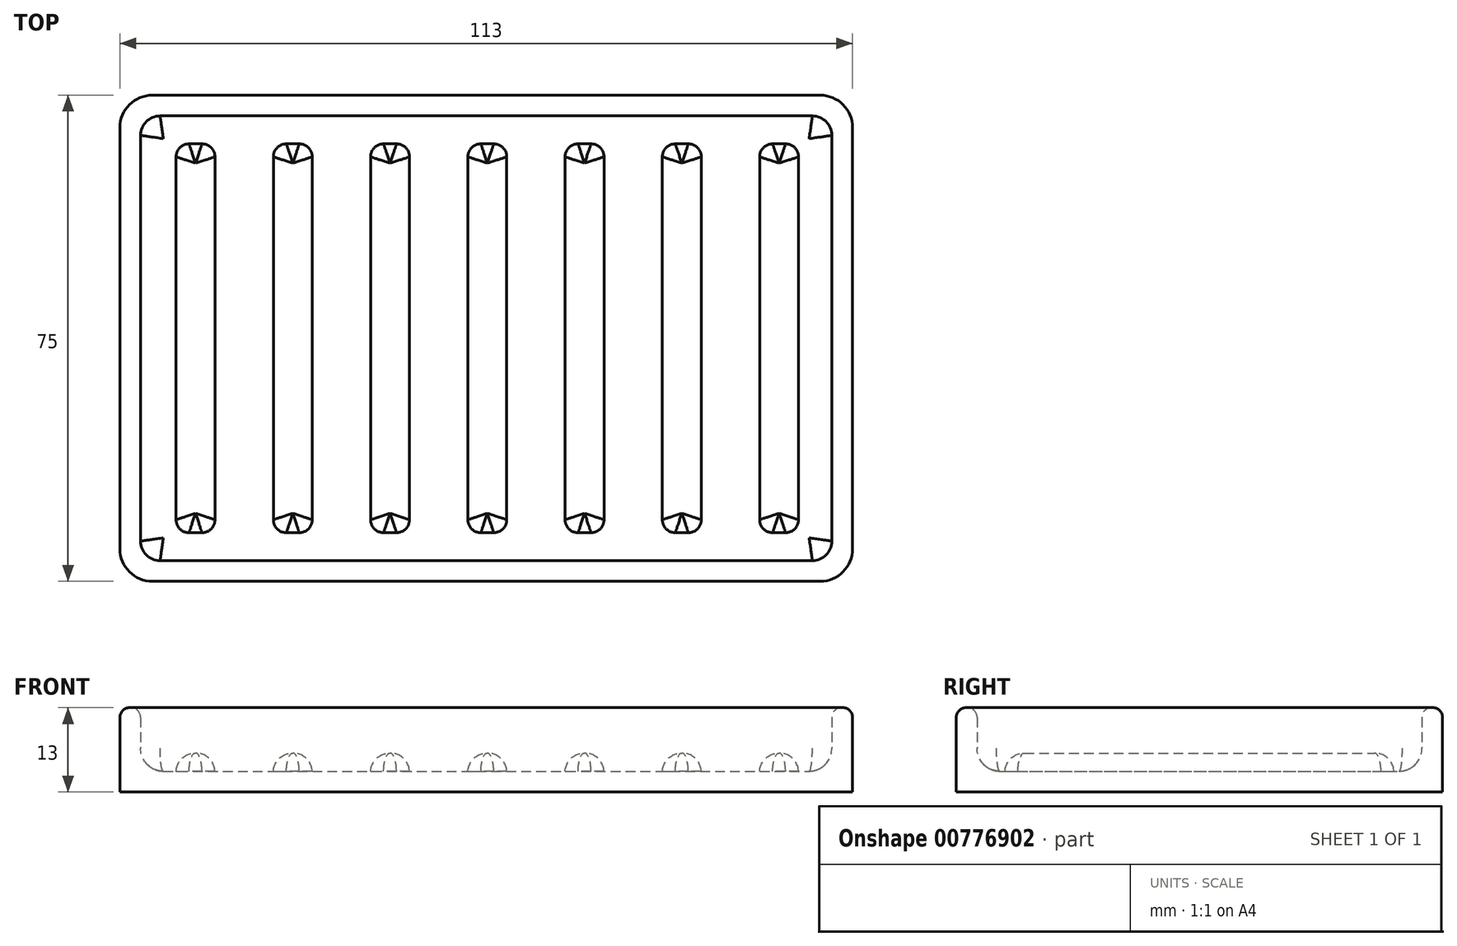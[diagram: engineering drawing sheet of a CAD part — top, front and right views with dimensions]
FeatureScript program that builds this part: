
annotation { "Feature Type Name" : "Feature", "Feature Type Description" : "" }
export const myFeature = defineFeature(function(context is Context, id is Id, definition is map)
    precondition{}
    {
        {
            var Q0;
            Q0=qCreatedBy(makeId("Top.planeOp"),FACE);
            var sketch = newSketch(context, id + "F0", { "sketchPlane" : qUnion([Q0])});
            skLineSegment(sketch, "E0.bottom", {"start": v(51.5, 37.5) * mm, "end": v(-51.5, 37.5) * mm});
            skLineSegment(sketch, "E0.top", {"start": v(51.5, -37.5) * mm, "end": v(-51.5, -37.5) * mm});
            skLineSegment(sketch, "E0.left", {"start": v(56.5, 32.5) * mm, "end": v(56.5, -32.5) * mm});
            skLineSegment(sketch, "E0.right", {"start": v(-56.5, 32.5) * mm, "end": v(-56.5, -32.5) * mm});
            skLineSegment(sketch, "E1.0", {"start": v(-53.3, 31.3) * mm, "end": v(-53.3, -31.3) * mm});
            skLineSegment(sketch, "E1.1", {"start": v(50.3, 34.3) * mm, "end": v(-50.3, 34.3) * mm});
            skLineSegment(sketch, "E1.2", {"start": v(53.3, 31.3) * mm, "end": v(53.3, -31.3) * mm});
            skLineSegment(sketch, "E1.3", {"start": v(50.3, -34.3) * mm, "end": v(-50.3, -34.3) * mm});
            skLineSegment(sketch, "E2.bottom", {"start": v(-45.84, 30) * mm, "end": v(-43.84, 30) * mm});
            skLineSegment(sketch, "E2.top", {"start": v(-45.84, -30) * mm, "end": v(-43.84, -30) * mm});
            skLineSegment(sketch, "E2.left", {"start": v(-47.84, 28) * mm, "end": v(-47.84, -28) * mm});
            skLineSegment(sketch, "E2.right", {"start": v(-41.84, 28) * mm, "end": v(-41.84, -28) * mm});
            skPoint(sketch, "E3.visualSharp", {"position": v(-56.5, 37.5) * mm});
            skArc(sketch, "E3.filletArc", {"start": v(-51.5, 37.5) * mm, "mid": v(-55.04, 36.04) * mm, "end": v(-56.5, 32.5) * mm});
            skPoint(sketch, "E4.visualSharp", {"position": v(-47.84, 30) * mm});
            skArc(sketch, "E4.filletArc", {"start": v(-45.84, 30) * mm, "mid": v(-47.25, 29.4) * mm, "end": v(-47.84, 28) * mm});
            skPoint(sketch, "E5.visualSharp", {"position": v(-47.84, -30) * mm});
            skArc(sketch, "E5.filletArc", {"start": v(-47.84, -28) * mm, "mid": v(-47.25, -29.42) * mm, "end": v(-45.84, -30) * mm});
            skPoint(sketch, "E6.visualSharp", {"position": v(-41.84, 30) * mm});
            skArc(sketch, "E6.filletArc", {"start": v(-41.84, 28) * mm, "mid": v(-42.42, 29.4) * mm, "end": v(-43.84, 30) * mm});
            skPoint(sketch, "E7.visualSharp", {"position": v(-41.84, -30) * mm});
            skArc(sketch, "E7.filletArc", {"start": v(-43.84, -30) * mm, "mid": v(-42.42, -29.42) * mm, "end": v(-41.84, -28) * mm});
            skPoint(sketch, "E8.1.0.0", {"position": v(-32.84, 30) * mm});
            skPoint(sketch, "E8.1.0.1", {"position": v(-32.84, -30) * mm});
            skPoint(sketch, "E8.1.0.2", {"position": v(-26.84, 30) * mm});
            skPoint(sketch, "E8.1.0.3", {"position": v(-26.84, -30) * mm});
            skLineSegment(sketch, "E8.1.0.4", {"start": v(-30.84, 30) * mm, "end": v(-28.84, 30) * mm});
            skLineSegment(sketch, "E8.1.0.5", {"start": v(-30.84, -30) * mm, "end": v(-28.84, -30) * mm});
            skLineSegment(sketch, "E8.1.0.6", {"start": v(-32.84, 28) * mm, "end": v(-32.84, -28) * mm});
            skLineSegment(sketch, "E8.1.0.7", {"start": v(-26.84, 28) * mm, "end": v(-26.84, -28) * mm});
            skArc(sketch, "E8.1.0.8", {"start": v(-30.84, 30) * mm, "mid": v(-32.25, 29.4) * mm, "end": v(-32.84, 28) * mm});
            skArc(sketch, "E8.1.0.9", {"start": v(-32.84, -28) * mm, "mid": v(-32.25, -29.42) * mm, "end": v(-30.84, -30) * mm});
            skArc(sketch, "E8.1.0.10", {"start": v(-26.84, 28) * mm, "mid": v(-27.42, 29.4) * mm, "end": v(-28.84, 30) * mm});
            skArc(sketch, "E8.1.0.11", {"start": v(-28.84, -30) * mm, "mid": v(-27.42, -29.42) * mm, "end": v(-26.84, -28) * mm});
            skPoint(sketch, "E8.2.0.0", {"position": v(-17.84, 30) * mm});
            skPoint(sketch, "E8.2.0.1", {"position": v(-17.84, -30) * mm});
            skPoint(sketch, "E8.2.0.2", {"position": v(-11.84, 30) * mm});
            skPoint(sketch, "E8.2.0.3", {"position": v(-11.84, -30) * mm});
            skLineSegment(sketch, "E8.2.0.4", {"start": v(-15.84, 30) * mm, "end": v(-13.84, 30) * mm});
            skLineSegment(sketch, "E8.2.0.5", {"start": v(-15.84, -30) * mm, "end": v(-13.84, -30) * mm});
            skLineSegment(sketch, "E8.2.0.6", {"start": v(-17.84, 28) * mm, "end": v(-17.84, -28) * mm});
            skLineSegment(sketch, "E8.2.0.7", {"start": v(-11.84, 28) * mm, "end": v(-11.84, -28) * mm});
            skArc(sketch, "E8.2.0.8", {"start": v(-15.84, 30) * mm, "mid": v(-17.25, 29.4) * mm, "end": v(-17.84, 28) * mm});
            skArc(sketch, "E8.2.0.9", {"start": v(-17.84, -28) * mm, "mid": v(-17.25, -29.42) * mm, "end": v(-15.84, -30) * mm});
            skArc(sketch, "E8.2.0.10", {"start": v(-11.84, 28) * mm, "mid": v(-12.42, 29.4) * mm, "end": v(-13.84, 30) * mm});
            skArc(sketch, "E8.2.0.11", {"start": v(-13.84, -30) * mm, "mid": v(-12.42, -29.42) * mm, "end": v(-11.84, -28) * mm});
            skPoint(sketch, "E8.3.0.0", {"position": v(-2.84, 30) * mm});
            skPoint(sketch, "E8.3.0.1", {"position": v(-2.84, -30) * mm});
            skPoint(sketch, "E8.3.0.2", {"position": v(3.16, 30) * mm});
            skPoint(sketch, "E8.3.0.3", {"position": v(3.16, -30) * mm});
            skLineSegment(sketch, "E8.3.0.4", {"start": v(-0.84, 30) * mm, "end": v(1.16, 30) * mm});
            skLineSegment(sketch, "E8.3.0.5", {"start": v(-0.84, -30) * mm, "end": v(1.16, -30) * mm});
            skLineSegment(sketch, "E8.3.0.6", {"start": v(-2.84, 28) * mm, "end": v(-2.84, -28) * mm});
            skLineSegment(sketch, "E8.3.0.7", {"start": v(3.16, 28) * mm, "end": v(3.16, -28) * mm});
            skArc(sketch, "E8.3.0.8", {"start": v(-0.84, 30) * mm, "mid": v(-2.25, 29.4) * mm, "end": v(-2.84, 28) * mm});
            skArc(sketch, "E8.3.0.9", {"start": v(-2.84, -28) * mm, "mid": v(-2.25, -29.42) * mm, "end": v(-0.84, -30) * mm});
            skArc(sketch, "E8.3.0.10", {"start": v(3.16, 28) * mm, "mid": v(2.58, 29.4) * mm, "end": v(1.16, 30) * mm});
            skArc(sketch, "E8.3.0.11", {"start": v(1.16, -30) * mm, "mid": v(2.58, -29.42) * mm, "end": v(3.16, -28) * mm});
            skPoint(sketch, "E8.4.0.0", {"position": v(12.16, 30) * mm});
            skPoint(sketch, "E8.4.0.1", {"position": v(12.16, -30) * mm});
            skPoint(sketch, "E8.4.0.2", {"position": v(18.16, 30) * mm});
            skPoint(sketch, "E8.4.0.3", {"position": v(18.16, -30) * mm});
            skLineSegment(sketch, "E8.4.0.4", {"start": v(14.16, 30) * mm, "end": v(16.16, 30) * mm});
            skLineSegment(sketch, "E8.4.0.5", {"start": v(14.16, -30) * mm, "end": v(16.16, -30) * mm});
            skLineSegment(sketch, "E8.4.0.6", {"start": v(12.16, 28) * mm, "end": v(12.16, -28) * mm});
            skLineSegment(sketch, "E8.4.0.7", {"start": v(18.16, 28) * mm, "end": v(18.16, -28) * mm});
            skArc(sketch, "E8.4.0.8", {"start": v(14.16, 30) * mm, "mid": v(12.75, 29.4) * mm, "end": v(12.16, 28) * mm});
            skArc(sketch, "E8.4.0.9", {"start": v(12.16, -28) * mm, "mid": v(12.75, -29.42) * mm, "end": v(14.16, -30) * mm});
            skArc(sketch, "E8.4.0.10", {"start": v(18.16, 28) * mm, "mid": v(17.58, 29.4) * mm, "end": v(16.16, 30) * mm});
            skArc(sketch, "E8.4.0.11", {"start": v(16.16, -30) * mm, "mid": v(17.58, -29.42) * mm, "end": v(18.16, -28) * mm});
            skPoint(sketch, "E8.5.0.0", {"position": v(27.16, 30) * mm});
            skPoint(sketch, "E8.5.0.1", {"position": v(27.16, -30) * mm});
            skPoint(sketch, "E8.5.0.2", {"position": v(33.16, 30) * mm});
            skPoint(sketch, "E8.5.0.3", {"position": v(33.16, -30) * mm});
            skLineSegment(sketch, "E8.5.0.4", {"start": v(29.16, 30) * mm, "end": v(31.16, 30) * mm});
            skLineSegment(sketch, "E8.5.0.5", {"start": v(29.16, -30) * mm, "end": v(31.16, -30) * mm});
            skLineSegment(sketch, "E8.5.0.6", {"start": v(27.16, 28) * mm, "end": v(27.16, -28) * mm});
            skLineSegment(sketch, "E8.5.0.7", {"start": v(33.16, 28) * mm, "end": v(33.16, -28) * mm});
            skArc(sketch, "E8.5.0.8", {"start": v(29.16, 30) * mm, "mid": v(27.75, 29.4) * mm, "end": v(27.16, 28) * mm});
            skArc(sketch, "E8.5.0.9", {"start": v(27.16, -28) * mm, "mid": v(27.75, -29.42) * mm, "end": v(29.16, -30) * mm});
            skArc(sketch, "E8.5.0.10", {"start": v(33.16, 28) * mm, "mid": v(32.58, 29.4) * mm, "end": v(31.16, 30) * mm});
            skArc(sketch, "E8.5.0.11", {"start": v(31.16, -30) * mm, "mid": v(32.58, -29.42) * mm, "end": v(33.16, -28) * mm});
            skPoint(sketch, "E8.6.0.0", {"position": v(42.16, 30) * mm});
            skPoint(sketch, "E8.6.0.1", {"position": v(42.16, -30) * mm});
            skPoint(sketch, "E8.6.0.2", {"position": v(48.16, 30) * mm});
            skPoint(sketch, "E8.6.0.3", {"position": v(48.16, -30) * mm});
            skLineSegment(sketch, "E8.6.0.4", {"start": v(44.16, 30) * mm, "end": v(46.16, 30) * mm});
            skLineSegment(sketch, "E8.6.0.5", {"start": v(44.16, -30) * mm, "end": v(46.16, -30) * mm});
            skLineSegment(sketch, "E8.6.0.6", {"start": v(42.16, 28) * mm, "end": v(42.16, -28) * mm});
            skLineSegment(sketch, "E8.6.0.7", {"start": v(48.16, 28) * mm, "end": v(48.16, -28) * mm});
            skArc(sketch, "E8.6.0.8", {"start": v(44.16, 30) * mm, "mid": v(42.75, 29.4) * mm, "end": v(42.16, 28) * mm});
            skArc(sketch, "E8.6.0.9", {"start": v(42.16, -28) * mm, "mid": v(42.75, -29.42) * mm, "end": v(44.16, -30) * mm});
            skArc(sketch, "E8.6.0.10", {"start": v(48.16, 28) * mm, "mid": v(47.58, 29.4) * mm, "end": v(46.16, 30) * mm});
            skArc(sketch, "E8.6.0.11", {"start": v(46.16, -30) * mm, "mid": v(47.58, -29.42) * mm, "end": v(48.16, -28) * mm});
            skLineSegment(sketch, "E8.direction1", {"start": v(-47.84, -30) * mm, "end": v(-32.84, -30) * mm, "construction": true});
            skPoint(sketch, "E9.visualSharp", {"position": v(-56.5, -37.5) * mm});
            skArc(sketch, "E9.filletArc", {"start": v(-56.5, -32.5) * mm, "mid": v(-55.04, -36.04) * mm, "end": v(-51.5, -37.5) * mm});
            skPoint(sketch, "E10.visualSharp", {"position": v(56.5, -37.5) * mm});
            skArc(sketch, "E10.filletArc", {"start": v(51.5, -37.5) * mm, "mid": v(55.04, -36.04) * mm, "end": v(56.5, -32.5) * mm});
            skPoint(sketch, "E11.visualSharp", {"position": v(56.5, 37.5) * mm});
            skArc(sketch, "E11.filletArc", {"start": v(56.5, 32.5) * mm, "mid": v(55.04, 36.04) * mm, "end": v(51.5, 37.5) * mm});
            skPoint(sketch, "E12.visualSharp", {"position": v(-53.3, -34.3) * mm});
            skArc(sketch, "E12.filletArc", {"start": v(-53.3, -31.3) * mm, "mid": v(-52.42, -33.42) * mm, "end": v(-50.3, -34.3) * mm});
            skPoint(sketch, "E13.visualSharp", {"position": v(-53.3, 34.3) * mm});
            skArc(sketch, "E13.filletArc", {"start": v(-50.3, 34.3) * mm, "mid": v(-52.42, 33.42) * mm, "end": v(-53.3, 31.3) * mm});
            skPoint(sketch, "E14.visualSharp", {"position": v(53.3, 34.3) * mm});
            skArc(sketch, "E14.filletArc", {"start": v(53.3, 31.3) * mm, "mid": v(52.42, 33.42) * mm, "end": v(50.3, 34.3) * mm});
            skPoint(sketch, "E15.visualSharp", {"position": v(53.3, -34.3) * mm});
            skArc(sketch, "E15.filletArc", {"start": v(50.3, -34.3) * mm, "mid": v(52.42, -33.42) * mm, "end": v(53.3, -31.3) * mm});
            skSolve(sketch);
        }
        {
            var Q0;
            Q0=makeQuery(id+"F0.imprint","IMPRINT",FACE,{"disambiguationData":[TD([[makeQuery(id+"F0.imprint","IMPRINT",EDGE,{"derivedFrom":sQuery(id+"F0.wireOp",EDGE,"E1.0")}),1.0]])]});
            var Q1;
            Q1=makeQuery(id+"F0.imprint","IMPRINT",FACE,{"disambiguationData":[TD([[makeQuery(id+"F0.imprint","IMPRINT",EDGE,{"derivedFrom":sQuery(id+"F0.wireOp",EDGE,"E8.6.0.4")}),-1.0]])]});
            var Q2;
            Q2=makeQuery(id+"F0.imprint","IMPRINT",FACE,{"disambiguationData":[TD([[makeQuery(id+"F0.imprint","IMPRINT",EDGE,{"derivedFrom":sQuery(id+"F0.wireOp",EDGE,"E8.5.0.4")}),-1.0]])]});
            var Q3;
            Q3=makeQuery(id+"F0.imprint","IMPRINT",FACE,{"disambiguationData":[TD([[makeQuery(id+"F0.imprint","IMPRINT",EDGE,{"derivedFrom":sQuery(id+"F0.wireOp",EDGE,"E8.4.0.4")}),-1.0]])]});
            var Q4;
            Q4=makeQuery(id+"F0.imprint","IMPRINT",FACE,{"disambiguationData":[TD([[makeQuery(id+"F0.imprint","IMPRINT",EDGE,{"derivedFrom":sQuery(id+"F0.wireOp",EDGE,"E8.3.0.4")}),-1.0]])]});
            var Q5;
            Q5=makeQuery(id+"F0.imprint","IMPRINT",FACE,{"disambiguationData":[TD([[makeQuery(id+"F0.imprint","IMPRINT",EDGE,{"derivedFrom":sQuery(id+"F0.wireOp",EDGE,"E8.2.0.4")}),-1.0]])]});
            var Q6;
            Q6=makeQuery(id+"F0.imprint","IMPRINT",FACE,{"disambiguationData":[TD([[makeQuery(id+"F0.imprint","IMPRINT",EDGE,{"derivedFrom":sQuery(id+"F0.wireOp",EDGE,"E8.1.0.4")}),-1.0]])]});
            var Q7;
            Q7=makeQuery(id+"F0.imprint","IMPRINT",FACE,{"disambiguationData":[TD([[makeQuery(id+"F0.imprint","IMPRINT",EDGE,{"derivedFrom":sQuery(id+"F0.wireOp",EDGE,"E2.bottom")}),-1.0]])]});
            var Q8;
            Q8=makeQuery(id+"F0.imprint","IMPRINT",FACE,{"disambiguationData":[TD([[makeQuery(id+"F0.imprint","IMPRINT",EDGE,{"derivedFrom":sQuery(id+"F0.wireOp",EDGE,"E0.bottom")}),1.0]])]});
            extrude(context, id + "F1", {"entities" : qUnion([Q0, Q1, Q2, Q3, Q4, Q5, Q6, Q7, Q8]), "depth" : 3.2 * mm, "offsetDistance" : 25 * mm});
        }
        {
            var Q0;
            Q0=makeQuery(id+"F0.imprint","IMPRINT",FACE,{"disambiguationData":[TD([[makeQuery(id+"F0.imprint","IMPRINT",EDGE,{"derivedFrom":sQuery(id+"F0.wireOp",EDGE,"E2.bottom")}),-1.0]])]});
            extrude(context, id + "F2", {"entities" : qUnion([Q0]), "operationType" : NewBodyOperationType.ADD, "depth" : 6 * mm, "offsetDistance" : 25 * mm});
        }
        {
            var Q0;
            Q0=makeQuery(id+"F0.imprint","IMPRINT",FACE,{"disambiguationData":[TD([[makeQuery(id+"F0.imprint","IMPRINT",EDGE,{"derivedFrom":sQuery(id+"F0.wireOp",EDGE,"E8.1.0.4")}),-1.0]])]});
            var Q1;
            Q1=makeQuery(id+"F0.imprint","IMPRINT",FACE,{"disambiguationData":[TD([[makeQuery(id+"F0.imprint","IMPRINT",EDGE,{"derivedFrom":sQuery(id+"F0.wireOp",EDGE,"E8.2.0.4")}),-1.0]])]});
            var Q2;
            Q2=makeQuery(id+"F0.imprint","IMPRINT",FACE,{"disambiguationData":[TD([[makeQuery(id+"F0.imprint","IMPRINT",EDGE,{"derivedFrom":sQuery(id+"F0.wireOp",EDGE,"E8.3.0.4")}),-1.0]])]});
            var Q3;
            Q3=makeQuery(id+"F0.imprint","IMPRINT",FACE,{"disambiguationData":[TD([[makeQuery(id+"F0.imprint","IMPRINT",EDGE,{"derivedFrom":sQuery(id+"F0.wireOp",EDGE,"E8.4.0.4")}),-1.0]])]});
            var Q4;
            Q4=makeQuery(id+"F0.imprint","IMPRINT",FACE,{"disambiguationData":[TD([[makeQuery(id+"F0.imprint","IMPRINT",EDGE,{"derivedFrom":sQuery(id+"F0.wireOp",EDGE,"E8.5.0.4")}),-1.0]])]});
            var Q5;
            Q5=makeQuery(id+"F0.imprint","IMPRINT",FACE,{"disambiguationData":[TD([[makeQuery(id+"F0.imprint","IMPRINT",EDGE,{"derivedFrom":sQuery(id+"F0.wireOp",EDGE,"E8.6.0.4")}),-1.0]])]});
            extrude(context, id + "F3", {"entities" : qUnion([Q0, Q1, Q2, Q3, Q4, Q5]), "operationType" : NewBodyOperationType.ADD, "depth" : 6 * mm, "offsetDistance" : 25 * mm});
        }
        {
            var Q0;
            Q0=makeQuery(id+"F2.opExtrude","CAP_EDGE",EDGE,{"disambiguationData":[OSD([sQuery(id+"F0.wireOp",EDGE,"E2.left")])],"isStart":false});
            var Q1;
            Q1=makeQuery(id+"F3.opExtrude","CAP_EDGE",EDGE,{"disambiguationData":[OSD([sQuery(id+"F0.wireOp",EDGE,"E8.1.0.6")])],"isStart":false});
            var Q2;
            Q2=makeQuery(id+"F3.opExtrude","CAP_EDGE",EDGE,{"disambiguationData":[OSD([sQuery(id+"F0.wireOp",EDGE,"E8.2.0.6")])],"isStart":false});
            var Q3;
            Q3=makeQuery(id+"F3.opExtrude","CAP_EDGE",EDGE,{"disambiguationData":[OSD([sQuery(id+"F0.wireOp",EDGE,"E8.3.0.6")])],"isStart":false});
            var Q4;
            Q4=makeQuery(id+"F3.opExtrude","CAP_EDGE",EDGE,{"disambiguationData":[OSD([sQuery(id+"F0.wireOp",EDGE,"E8.4.0.6")])],"isStart":false});
            var Q5;
            Q5=makeQuery(id+"F3.opExtrude","CAP_EDGE",EDGE,{"disambiguationData":[OSD([sQuery(id+"F0.wireOp",EDGE,"E8.5.0.6")])],"isStart":false});
            var Q6;
            Q6=makeQuery(id+"F3.opExtrude","CAP_EDGE",EDGE,{"disambiguationData":[OSD([sQuery(id+"F0.wireOp",EDGE,"E8.6.0.6")])],"isStart":false});
            fillet(context, id + "F4", {"entities" : qUnion([Q0, Q1, Q2, Q3, Q4, Q5, Q6]), "radius" : 3 * mm, "tangentPropagation" : true, "allowEdgeOverflow" : false});
        }
        {
            var Q0;
            Q0=makeQuery(id+"F0.imprint","IMPRINT",FACE,{"disambiguationData":[TD([[makeQuery(id+"F0.imprint","IMPRINT",EDGE,{"derivedFrom":sQuery(id+"F0.wireOp",EDGE,"E0.bottom")}),1.0]])]});
            extrude(context, id + "F5", {"entities" : qUnion([Q0]), "operationType" : NewBodyOperationType.ADD, "depth" : 13 * mm, "offsetDistance" : 25 * mm});
        }
        {
            var Q0;
            Q0=makeQuery(id+"F5.opExtrude","CAP_EDGE",EDGE,{"disambiguationData":[OSD([sQuery(id+"F0.wireOp",EDGE,"E0.top")])],"isStart":false});
            var Q1;
            Q1=makeQuery(id+"F5.opExtrude","CAP_EDGE",EDGE,{"disambiguationData":[OSD([sQuery(id+"F0.wireOp",EDGE,"E1.1")])],"isStart":false});
            fillet(context, id + "F6", {"entities" : qUnion([Q0, Q1]), "radius" : 1.5 * mm, "tangentPropagation" : true, "allowEdgeOverflow" : false});
        }
        {
            var Q0;
            Q0=makeQuery(id+"F5.boolean.opBoolean","INTERSECT",EDGE,{"derivedFrom":[makeQuery(id+"F1.opExtrude","CAP_FACE",FACE,{"disambiguationData":[OSD([sQuery(id+"F0.wireOp",EDGE,"E0.bottom"),sQuery(id+"F0.wireOp",EDGE,"E0.top"),sQuery(id+"F0.wireOp",EDGE,"E0.left"),sQuery(id+"F0.wireOp",EDGE,"E0.right"),sQuery(id+"F0.wireOp",EDGE,"E3.filletArc"),sQuery(id+"F0.wireOp",EDGE,"E9.filletArc"),sQuery(id+"F0.wireOp",EDGE,"E10.filletArc"),sQuery(id+"F0.wireOp",EDGE,"E11.filletArc")])],"isStart":false}),makeQuery(id+"F5.opExtrude","SWEPT_FACE",FACE,{"disambiguationData":[OSD([sQuery(id+"F0.wireOp",EDGE,"E1.0")])]})]});
            fillet(context, id + "F7", {"entities" : qUnion([Q0]), "radius" : 3.5 * mm, "tangentPropagation" : true, "allowEdgeOverflow" : false});
        }
    });
